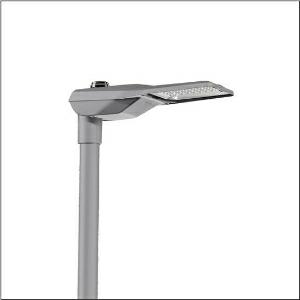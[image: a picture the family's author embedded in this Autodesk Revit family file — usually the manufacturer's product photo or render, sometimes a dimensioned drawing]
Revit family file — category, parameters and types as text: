
# Revit family: streetlight_sl_21_mini___st1_0a_5xe6d27n08jb_0e68
name_source: partatom
category: Lighting Fixtures
units: mm (PartAtom-declared; Revit-internal decimal feet)

## family parameters
Cut with Voids When Loaded = No
Host = Face
Light Source = No
Part Type = Normal
Room Calculation Point = No
Round Connector Dimension = Use Diameter
Shared = No

## types (1)
- --- (1 x LED, 10620 lm, 87.3 W, 2200K)
    Apparent Load = 87 VA
    CIE Flux Codes = 40 73 97 100 100
    Color Rendering = 70
    Color Temperature = 2200K
    Default Elevation = 1800 mm
    Description = Streetlight SL 21 mini, mast luminaire, primary light control with lens, of PMMA, primary optical cover: cover, of toughened safety glass, transparent, light distribution: ST1.0a, light emission: direct distribution, primary light characteristic: asymmetric, installation type: side-entry, LED, 3G 2.5mm², High Power LED, rated luminous flux: 10.620lm, luminous efficacy: 122lm/W, light colour: 722, colour temperature: 2200K, control gear: NEMA (7pin), control: overheat protection, pre-setting: linear dimming characteristic, constant luminous flux control, time-dependent luminous flux control, flexible luminous flux parameterisation, mains connection: 230..240V, AC, 50/60Hz, connection cable pre-assembled, cable length: 10,5m, wiring characteristics: H05VV-F, start of lifetime: 87W, end of service life: 90W, reduction: 40W, luminaire housing, of diecast aluminium (EN AC-44300), powder-coated, Siteco® metallic grey (DB 702S), corrosivity category C5 mid according to DIN EN ISO 12944, multi-level sealing system, sealing non-destructively replaceable, inclination adjustable: 0°, 5°, 10°, 15°, length: 628mm, width: 235mm, height: 110mm, spigot size: 42mm (side-entry), mounting height: 4..8m, protection rating (complete): IP66, insulation class (complete): insulation class I (protective earthing), certification: CE, ENEC, ENEC+, VDE, impact resistance: IK10, permissible operating ambient temperature for outdoor applications: -40..+50°C, standard-compliant lighting for roads and squares, packaging unit: 1 piece

Light Distribution: ST1.0a
    Height = 110 mm
    Lamp = 1 x LED
    Lamp Light Flux = 10620 lm
    Lamp Power = 87.3 W
    Lamp count = 1
    Length = 625 mm
    Luminous efficacy = 122 lm/W
    Manufacturer = Siteco
    ModVariant = No
    Model = 5XE6D27N08JB
    Number of Poles = 1
    OnlyDefault = Yes
    Power Factor = 1
    Product Name = Streetlight SL 21 mini | ST1.0a
    Product group = mast luminaire | pylon top
    ProductGroupID = 6100
    Protection Class = Protection class I
    Protection Degree = IP 66
    RLX_Detail_Level = 1
    RLX_Emergency_Light_Flux = 0 lm
    RLX_Emergency_Type = 0
    RLX_Emergency_Type_DB = No
    RlxData = <blob elided: 25993 chars, md5=f2b6bbd5>
    Socket = socket
    Standby Power = 0 W
    System Light Flux = 10620 lm
    System Power = 87 W
    Type Comments = factory setting: luminous flux: 100 % | dim-lin: 254 | 915 mA
    Type Image = l_1294379.jpg
    URL = http://relux.com
    VarID = @adj_135402
    Voltage = 0 V
    Weight = 0.00 kg
    Width = 234 mm

## geometry (parser evidence)
native form markers: Blend x4, Sweep x9
no freeform markers — native parametric forms only
